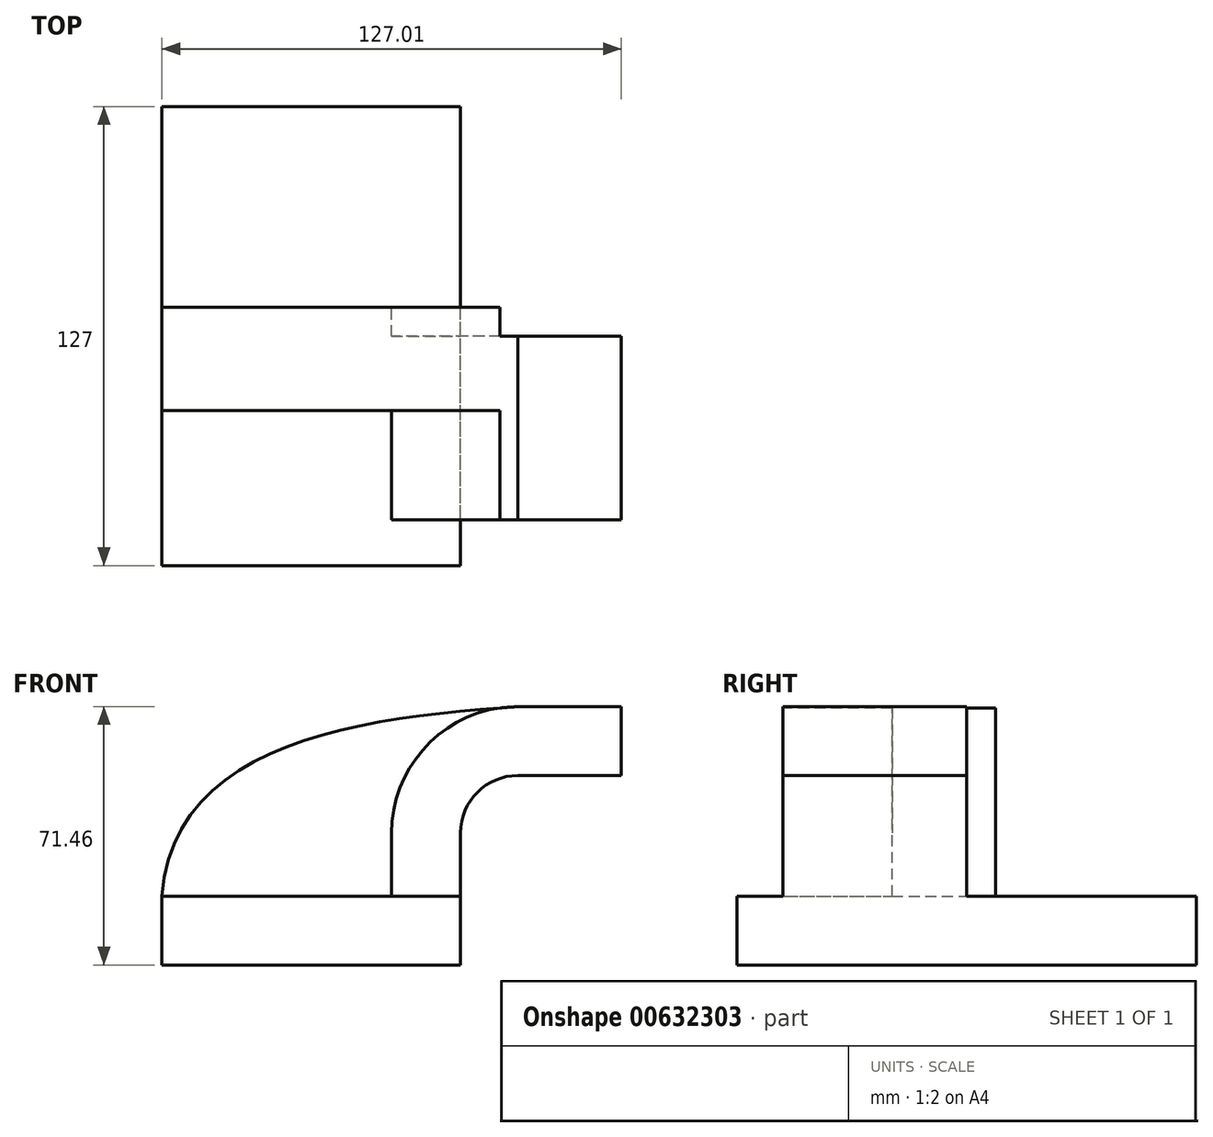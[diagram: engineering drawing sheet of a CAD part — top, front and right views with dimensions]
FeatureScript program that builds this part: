
annotation { "Feature Type Name" : "Feature", "Feature Type Description" : "" }
export const myFeature = defineFeature(function(context is Context, id is Id, definition is map)
    precondition{}
    {
        {
            var Q0;
            Q0=qCreatedBy(makeId("Front.planeOp"),FACE);
            var sketch = newSketch(context, id + "F0", { "sketchPlane" : qUnion([Q0])});
            skLineSegment(sketch, "E0.bottom", {"start": v(-41.28, 9.52) * mm, "end": v(41.28, 9.53) * mm});
            skLineSegment(sketch, "E0.top", {"start": v(-41.28, -9.53) * mm, "end": v(41.28, -9.53) * mm});
            skLineSegment(sketch, "E0.left", {"start": v(-41.28, 9.52) * mm, "end": v(-41.28, -9.53) * mm});
            skLineSegment(sketch, "E0.right", {"start": v(41.28, 9.53) * mm, "end": v(41.28, -9.52) * mm});
            skPoint(sketch, "E0.middle", {"position": v(0, 0) * mm});
            skLineSegment(sketch, "E1.bottom", {"start": v(111.12, 38.1) * mm, "end": v(60.32, 38.1) * mm});
            skLineSegment(sketch, "E1.top", {"start": v(111.12, 66.67) * mm, "end": v(60.32, 66.67) * mm});
            skLineSegment(sketch, "E1.left", {"start": v(111.12, 38.1) * mm, "end": v(111.12, 66.67) * mm});
            skLineSegment(sketch, "E1.right", {"start": v(60.32, 38.1) * mm, "end": v(60.32, 66.67) * mm});
            skPoint(sketch, "E1.middle", {"position": v(85.72, 52.39) * mm});
            skLineSegment(sketch, "E2", {"start": v(41.27, 9.53) * mm, "end": v(41.27, 27) * mm});
            skArc(sketch, "E3", {"start": v(41.27, 27) * mm, "mid": v(45.92, 38.23) * mm, "end": v(57.15, 42.88) * mm});
            skLineSegment(sketch, "E4", {"start": v(57.15, 42.88) * mm, "end": v(71.67, 42.88) * mm});
            skLineSegment(sketch, "E5.0", {"start": v(57.15, 61.93) * mm, "end": v(71.67, 61.93) * mm});
            skArc(sketch, "E5.1", {"start": v(22.22, 27) * mm, "mid": v(32.45, 51.7) * mm, "end": v(57.15, 61.93) * mm});
            skLineSegment(sketch, "E5.2", {"start": v(22.23, 9.53) * mm, "end": v(22.23, 27) * mm});
            skLineSegment(sketch, "E6", {"start": v(85.72, 38.1) * mm, "end": v(85.72, 66.67) * mm});
            skFitSpline(sketch, "E7", {"points": [v(-41.28, 9.52) * mm, v(57.15, 61.93) * mm], "startDerivative": vector(9.49, 128.5) * mm, "endDerivative": vector(129.67, 8.8) * mm});
            skSolve(sketch);
        }
        {
            var Q0;
            Q0=makeQuery(id+"F0.imprint","IMPRINT",FACE,{"disambiguationData":[TD([[makeQuery(id+"F0.imprint","IMPRINT",EDGE,{"derivedFrom":sQuery(id+"F0.wireOp",EDGE,"E0.top")}),1.0]])]});
            extrude(context, id + "F1", {"entities" : qUnion([Q0]), "endBound" : BoundingType.SYMMETRIC, "depth" : 127 * mm, "offsetDistance" : 25.4 * mm});
        }
        {
            var Q0;
            {var subQ1=sQuery(id+"F0.wireOp",EDGE,"E2");Q0=makeQuery(id+"F0.imprint","IMPRINT",FACE,{"disambiguationData":[TD([[makeQuery(id+"F0.imprint","IMPRINT",EDGE,{"derivedFrom":subQ1}),1.0]])]});}
            extrude(context, id + "F2", {"entities" : qUnion([Q0]), "operationType" : NewBodyOperationType.ADD, "depth" : 25.4 * mm, "offsetDistance" : 25.4 * mm});
        }
        {
            var Q0;
            Q0=makeQuery(id+"F2.opExtrude","CAP_FACE",FACE,{"disambiguationData":[OSD([sQuery(id+"F0.wireOp",EDGE,"E0.bottom"),sQuery(id+"F0.wireOp",EDGE,"E1.right"),sQuery(id+"F0.wireOp",EDGE,"E2"),sQuery(id+"F0.wireOp",EDGE,"E3"),sQuery(id+"F0.wireOp",EDGE,"E4"),sQuery(id+"F0.wireOp",EDGE,"E5.0"),sQuery(id+"F0.wireOp",EDGE,"E5.1"),sQuery(id+"F0.wireOp",EDGE,"E5.2"),sQuery(id+"F0.wireOp",EDGE,"E7")])],"isStart":false});
            extrude(context, id + "F3", {"entities" : qUnion([Q0]), "operationType" : NewBodyOperationType.ADD, "endBound" : BoundingType.SYMMETRIC, "depth" : 50.8 * mm, "offsetDistance" : 25.4 * mm});
        }
        {
            var Q0;
            {var subQ0=sQuery(id+"F0.wireOp",EDGE,"E1.right");Q0=makeQuery(id+"F3.boolean.opBoolean","MERGE",FACE,{"derivedFrom":[makeQuery(id+"F2.opExtrude","SWEPT_FACE",FACE,{"disambiguationData":[OSD([subQ0])]}),makeQuery(id+"F3.opExtrude","SWEPT_FACE",FACE,{"disambiguationData":[OSD([subQ0])]})]});}
            extrude(context, id + "F4", {"entities" : qUnion([Q0]), "operationType" : NewBodyOperationType.ADD, "depth" : 25.4 * mm, "offsetDistance" : 25.4 * mm});
        }
        {
            var Q0;
            {var subQ3=sQuery(id+"F0.wireOp",EDGE,"E5.2");Q0=makeQuery(id+"F0.imprint","IMPRINT",FACE,{"disambiguationData":[TD([[makeQuery(id+"F0.imprint","IMPRINT",EDGE,{"derivedFrom":subQ3}),1.0]])]});}
            extrude(context, id + "F5", {"entities" : qUnion([Q0]), "operationType" : NewBodyOperationType.ADD, "endBound" : BoundingType.SYMMETRIC, "depth" : 15.88 * mm, "offsetDistance" : 25.4 * mm});
        }
        {
            var Q0;
            Q0=makeQuery(id+"F5.opExtrude","CAP_FACE",FACE,{"disambiguationData":[OSD([sQuery(id+"F0.wireOp",EDGE,"E0.bottom"),sQuery(id+"F0.wireOp",EDGE,"E5.1"),sQuery(id+"F0.wireOp",EDGE,"E5.2"),sQuery(id+"F0.wireOp",EDGE,"E7")])],"isStart":false});
            extrude(context, id + "F6", {"entities" : qUnion([Q0]), "operationType" : NewBodyOperationType.ADD, "endBound" : BoundingType.SYMMETRIC, "depth" : 25.4 * mm, "offsetDistance" : 25.4 * mm});
        }
    });
